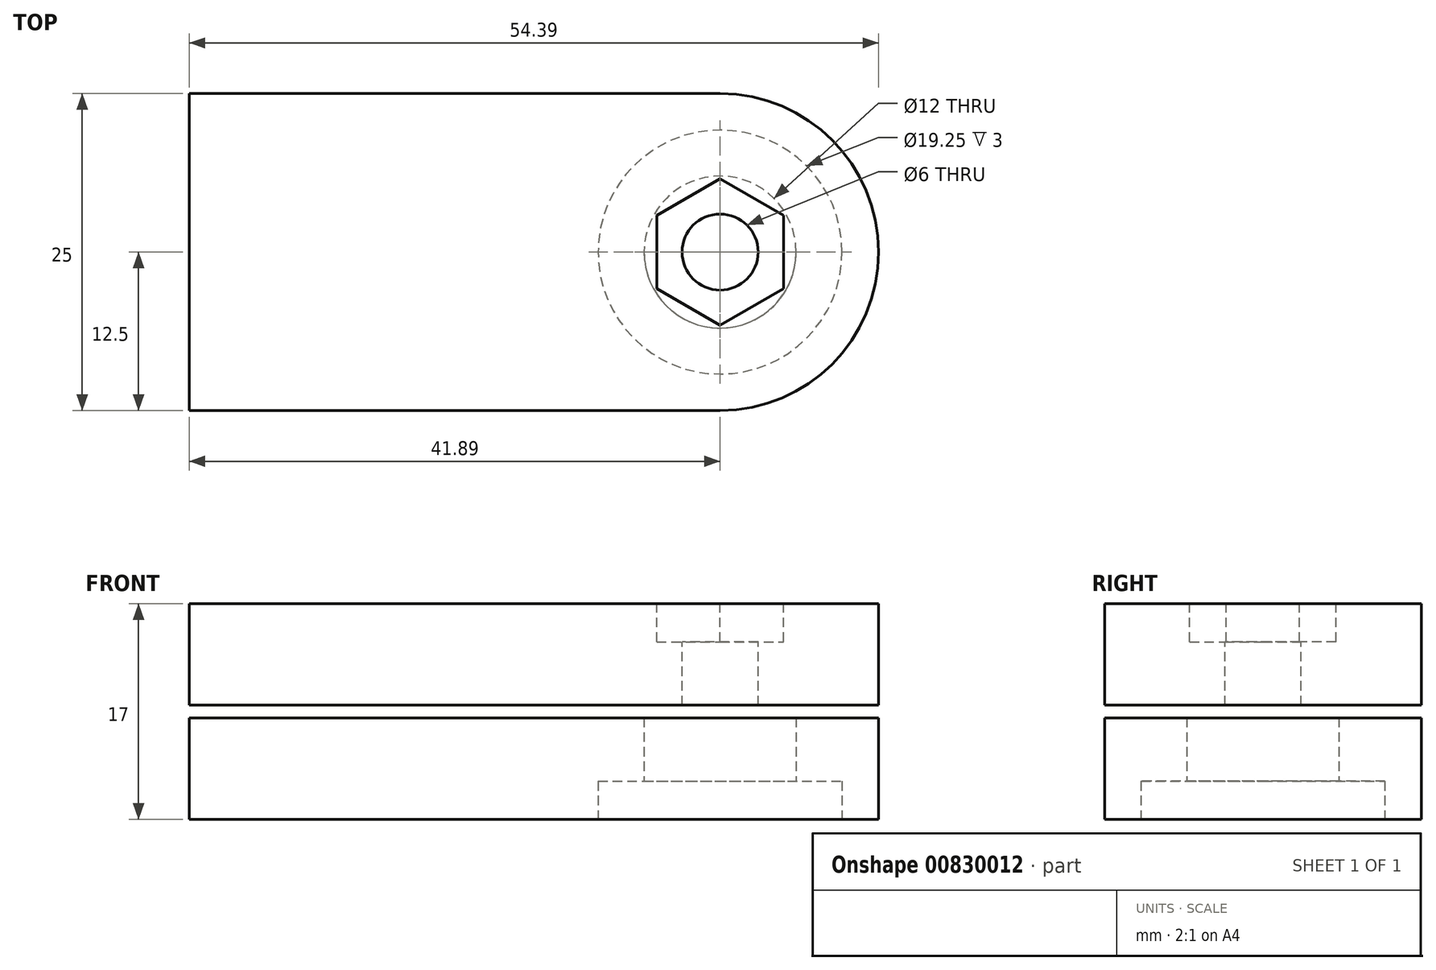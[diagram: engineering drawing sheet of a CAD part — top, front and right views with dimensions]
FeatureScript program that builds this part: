
annotation { "Feature Type Name" : "Feature", "Feature Type Description" : "" }
export const myFeature = defineFeature(function(context is Context, id is Id, definition is map)
    precondition{}
    {
        {
            var Q0;
            Q0=qCreatedBy(makeId("Top.planeOp"),FACE);
            var sketch = newSketch(context, id + "F0", { "sketchPlane" : qUnion([Q0])});
            skCircle(sketch, "E0", {"center": v(0, 0) * mm, "radius": 6 * mm});
            skArc(sketch, "E1", {"start": v(0, -12.5) * mm, "mid": v(12.5, 0) * mm, "end": v(0, 12.5) * mm});
            skLineSegment(sketch, "E2", {"start": v(0, 12.5) * mm, "end": v(-41.89, 12.5) * mm});
            skLineSegment(sketch, "E3", {"start": v(0, -12.5) * mm, "end": v(-41.89, -12.5) * mm});
            skLineSegment(sketch, "E4", {"start": v(-41.89, -12.5) * mm, "end": v(-41.89, 12.5) * mm});
            skSolve(sketch);
        }
        {
            var Q0;
            Q0 = qSketchRegion(id + "F0", true);
            extrude(context, id + "F1", {"entities" : qUnion([Q0]), "depth" : 8 * mm, "offsetDistance" : 25 * mm});
        }
        {
            var Q0;
            Q0=makeQuery(id+"F1.opExtrude","CAP_FACE",FACE,{"disambiguationData":[OSD([sQuery(id+"F0.wireOp",EDGE,"E0"),sQuery(id+"F0.wireOp",EDGE,"E1"),sQuery(id+"F0.wireOp",EDGE,"E2"),sQuery(id+"F0.wireOp",EDGE,"E3"),sQuery(id+"F0.wireOp",EDGE,"E4")])],"isStart":true});
            var sketch = newSketch(context, id + "F2", { "sketchPlane" : qUnion([Q0])});
            skCircle(sketch, "E5", {"center": v(0, 0) * mm, "radius": 9.62 * mm});
            skSolve(sketch);
        }
        {
            var Q0;
            Q0 = qSketchRegion(id + "F2", true);
            extrude(context, id + "F3", {"entities" : qUnion([Q0]), "operationType" : NewBodyOperationType.REMOVE, "oppositeDirection" : true, "depth" : 3 * mm, "offsetDistance" : 25 * mm});
        }
        {
            var Q0;
            Q0=makeQuery(id+"F1.opExtrude","CAP_FACE",FACE,{"disambiguationData":[OSD([sQuery(id+"F0.wireOp",EDGE,"E0"),sQuery(id+"F0.wireOp",EDGE,"E1"),sQuery(id+"F0.wireOp",EDGE,"E2"),sQuery(id+"F0.wireOp",EDGE,"E3"),sQuery(id+"F0.wireOp",EDGE,"E4")])],"isStart":false});
            cPlane(context, id + "F4", {"entities" : qUnion([Q0]), "cplaneType" : CPlaneType.OFFSET, "offset" : 1 * mm, "width" : 150 * mm, "height" : 150 * mm});
        }
        {
            var Q0;
            Q0=qCreatedBy(id+"F4.planeOp",FACE);
            var sketch = newSketch(context, id + "F5", { "sketchPlane" : qUnion([Q0])});
            skLineSegment(sketch, "E6.0", {"start": v(0, 12.5) * mm, "end": v(-41.89, 12.5) * mm});
            skArc(sketch, "E7.0", {"start": v(0, -12.5) * mm, "mid": v(12.5, 0) * mm, "end": v(0, 12.5) * mm});
            skLineSegment(sketch, "E8.0", {"start": v(0, -12.5) * mm, "end": v(-41.89, -12.5) * mm});
            skLineSegment(sketch, "E9.0", {"start": v(-41.89, -12.5) * mm, "end": v(-41.89, 12.5) * mm});
            skSolve(sketch);
        }
        {
            var Q0;
            Q0 = qSketchRegion(id + "F5", true);
            extrude(context, id + "F6", {"entities" : qUnion([Q0]), "depth" : 8 * mm, "offsetDistance" : 25 * mm});
        }
        {
            var Q0;
            Q0=makeQuery(id+"F6.opExtrude","CAP_FACE",FACE,{"disambiguationData":[OSD([sQuery(id+"F5.wireOp",EDGE,"E6.0"),sQuery(id+"F5.wireOp",EDGE,"E7.0"),sQuery(id+"F5.wireOp",EDGE,"E8.0"),sQuery(id+"F5.wireOp",EDGE,"E9.0")])],"isStart":false});
            var sketch = newSketch(context, id + "F7", { "sketchPlane" : qUnion([Q0])});
            skCircle(sketch, "E10", {"center": v(0, 0) * mm, "radius": 3 * mm});
            skSolve(sketch);
        }
        {
            var Q0;
            Q0 = qSketchRegion(id + "F7", true);
            extrude(context, id + "F8", {"entities" : qUnion([Q0]), "operationType" : NewBodyOperationType.REMOVE, "endBound" : BoundingType.THROUGH_ALL, "oppositeDirection" : true, "depth" : 25 * mm, "offsetDistance" : 25 * mm});
        }
        {
            var Q0;
            Q0=makeQuery(id+"F6.opExtrude","CAP_FACE",FACE,{"disambiguationData":[OSD([sQuery(id+"F5.wireOp",EDGE,"E6.0"),sQuery(id+"F5.wireOp",EDGE,"E7.0"),sQuery(id+"F5.wireOp",EDGE,"E8.0"),sQuery(id+"F5.wireOp",EDGE,"E9.0")])],"isStart":false});
            var sketch = newSketch(context, id + "F9", { "sketchPlane" : qUnion([Q0])});
            skCircle(sketch, "E11.cCircle", {"center": v(0, 0) * mm, "radius": 5 * mm, "construction": true});
            skLineSegment(sketch, "E11.0", {"start": v(5, 2.89) * mm, "end": v(5, -2.89) * mm});
            skLineSegment(sketch, "E11.1", {"start": v(5, -2.89) * mm, "end": v(0, -5.77) * mm});
            skLineSegment(sketch, "E11.2", {"start": v(0, -5.77) * mm, "end": v(-5, -2.89) * mm});
            skLineSegment(sketch, "E11.3", {"start": v(-5, -2.89) * mm, "end": v(-5, 2.89) * mm});
            skLineSegment(sketch, "E11.4", {"start": v(-5, 2.89) * mm, "end": v(0, 5.77) * mm});
            skLineSegment(sketch, "E11.5", {"start": v(0, 5.77) * mm, "end": v(5, 2.89) * mm});
            skPoint(sketch, "E11.0.midPoint", {"position": v(5, 0) * mm});
            skSolve(sketch);
        }
        {
            var Q0;
            Q0 = qSketchRegion(id + "F9", true);
            extrude(context, id + "F10", {"entities" : qUnion([Q0]), "operationType" : NewBodyOperationType.REMOVE, "oppositeDirection" : true, "depth" : 3 * mm, "offsetDistance" : 25 * mm});
        }
    });
